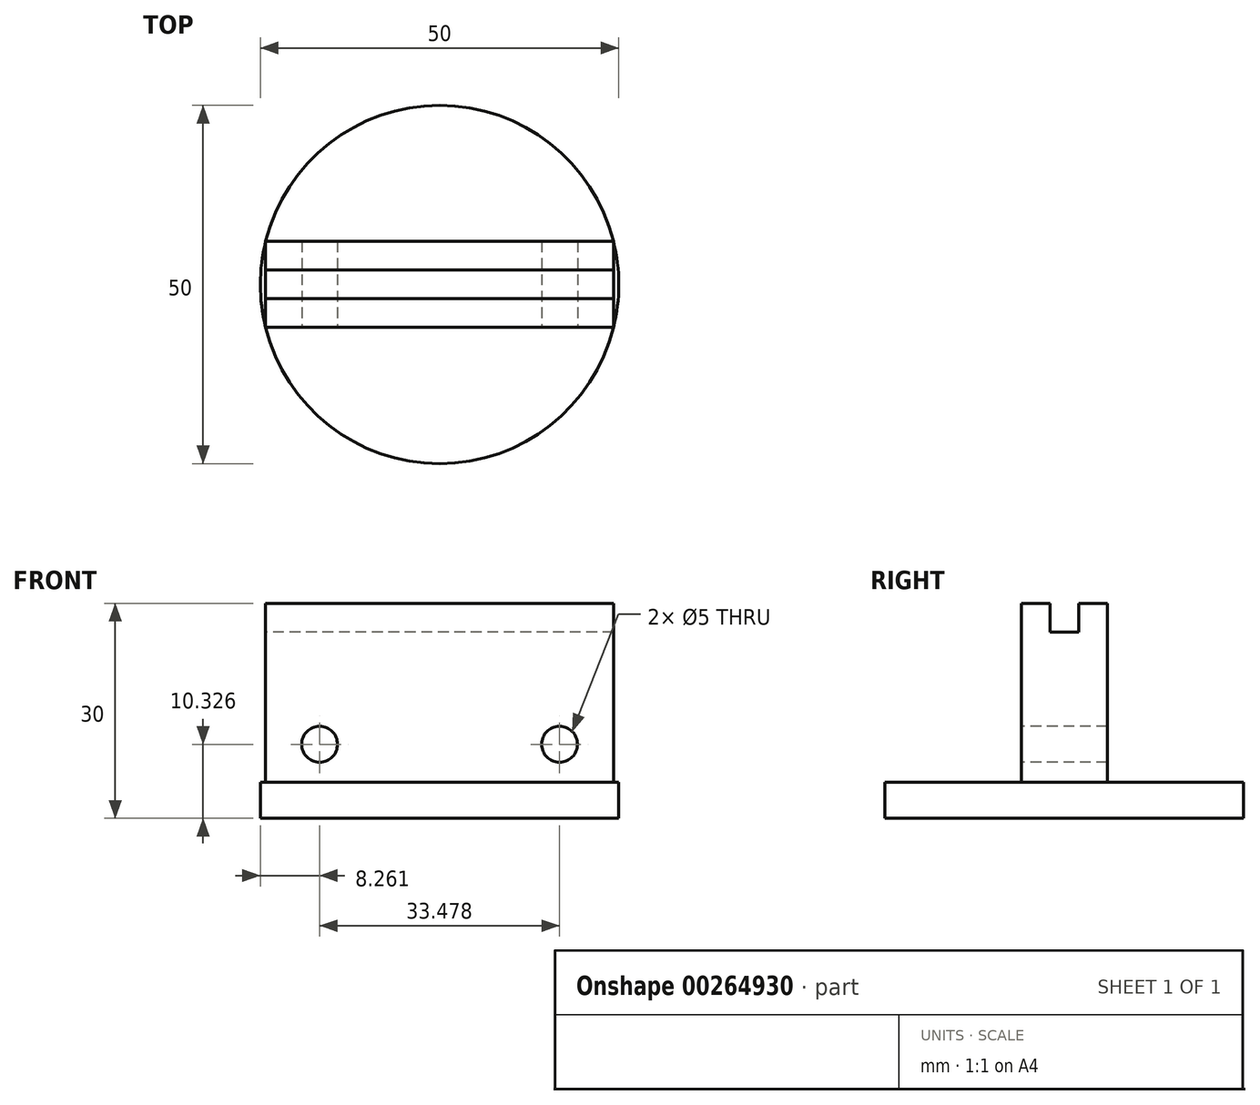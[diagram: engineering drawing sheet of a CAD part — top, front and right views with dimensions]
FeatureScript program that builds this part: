
annotation { "Feature Type Name" : "Feature", "Feature Type Description" : "" }
export const myFeature = defineFeature(function(context is Context, id is Id, definition is map)
    precondition{}
    {
        {
            var Q0;
            Q0=qCreatedBy(makeId("Top.planeOp"),FACE);
            var sketch = newSketch(context, id + "F0", { "sketchPlane" : qUnion([Q0])});
            skCircle(sketch, "E0", {"center": v(0, 0) * mm, "radius": 25 * mm});
            skSolve(sketch);
        }
        {
            var Q0;
            Q0 = qSketchRegion(id + "F0", true);
            extrude(context, id + "F1", {"entities" : qUnion([Q0]), "depth" : 5 * mm});
        }
        {
            var Q0;
            Q0=makeQuery(id+"F1.opExtrude","CAP_FACE",FACE,{"disambiguationData":[OSD([sQuery(id+"F0.wireOp",EDGE,"E0")])],"isStart":false});
            var sketch = newSketch(context, id + "F2", { "sketchPlane" : qUnion([Q0])});
            skLineSegment(sketch, "E1.bottom", {"start": v(-24.27, -6) * mm, "end": v(24.27, -6) * mm});
            skLineSegment(sketch, "E1.top", {"start": v(-24.27, 6) * mm, "end": v(24.27, 6) * mm});
            skLineSegment(sketch, "E1.left", {"start": v(-24.27, -6) * mm, "end": v(-24.27, 6) * mm});
            skLineSegment(sketch, "E1.right", {"start": v(24.27, -6) * mm, "end": v(24.27, 6) * mm});
            skSolve(sketch);
        }
        {
            var Q0;
            Q0 = qSketchRegion(id + "F2", true);
            extrude(context, id + "F3", {"entities" : qUnion([Q0]), "operationType" : NewBodyOperationType.ADD, "depth" : 25 * mm});
        }
        {
            var Q0;
            Q0=makeQuery(id+"F3.opExtrude","CAP_FACE",FACE,{"disambiguationData":[OSD([sQuery(id+"F2.wireOp",EDGE,"E1.bottom"),sQuery(id+"F2.wireOp",EDGE,"E1.top"),sQuery(id+"F2.wireOp",EDGE,"E1.left"),sQuery(id+"F2.wireOp",EDGE,"E1.right")])],"isStart":false});
            var sketch = newSketch(context, id + "F4", { "sketchPlane" : qUnion([Q0])});
            skLineSegment(sketch, "E2.bottom", {"start": v(24.27, 2) * mm, "end": v(-24.27, 2) * mm});
            skLineSegment(sketch, "E2.top", {"start": v(24.27, -2) * mm, "end": v(-24.27, -2) * mm});
            skLineSegment(sketch, "E2.left", {"start": v(24.27, 2) * mm, "end": v(24.27, -2) * mm});
            skLineSegment(sketch, "E2.right", {"start": v(-24.27, 2) * mm, "end": v(-24.27, -2) * mm});
            skPoint(sketch, "E2.middle", {"position": v(0, 0) * mm});
            skSolve(sketch);
        }
        {
            var Q0;
            Q0 = qSketchRegion(id + "F4", true);
            extrude(context, id + "F5", {"entities" : qUnion([Q0]), "operationType" : NewBodyOperationType.REMOVE, "oppositeDirection" : true, "depth" : 4 * mm});
        }
        {
            var Q0;
            Q0=makeQuery(id+"F3.opExtrude","SWEPT_FACE",FACE,{"disambiguationData":[OSD([sQuery(id+"F2.wireOp",EDGE,"E1.bottom")])]});
            var sketch = newSketch(context, id + "F6", { "sketchPlane" : qUnion([Q0])});
            skCircle(sketch, "E3", {"center": v(-16.74, 10.33) * mm, "radius": 2.5 * mm});
            skCircle(sketch, "E4.MirrorC", {"center": v(16.74, 10.33) * mm, "radius": 2.5 * mm});
            skSolve(sketch);
        }
        {
            var Q0;
            Q0 = qSketchRegion(id + "F6", true);
            extrude(context, id + "F7", {"entities" : qUnion([Q0]), "operationType" : NewBodyOperationType.REMOVE, "endBound" : BoundingType.THROUGH_ALL, "oppositeDirection" : true, "depth" : 25 * mm});
        }
    });
